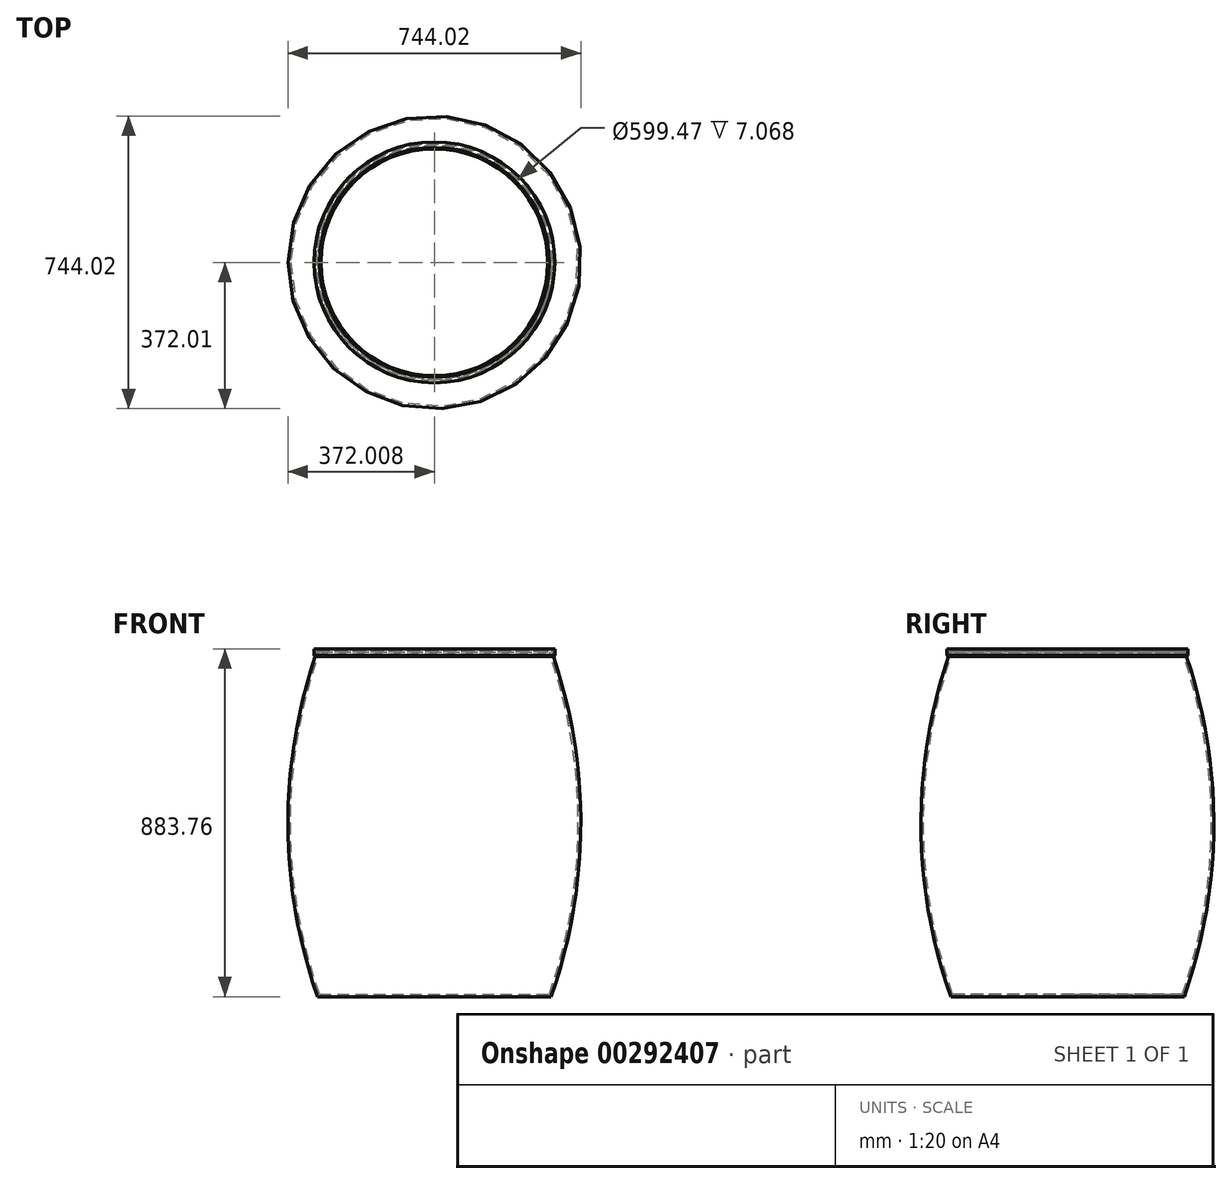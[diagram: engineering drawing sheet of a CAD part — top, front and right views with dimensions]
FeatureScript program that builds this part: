
annotation { "Feature Type Name" : "Feature", "Feature Type Description" : "" }
export const myFeature = defineFeature(function(context is Context, id is Id, definition is map)
    precondition{}
    {
        {
            var Q0;
            Q0=qCreatedBy(makeId("Front.planeOp"),FACE);
            var sketch = newSketch(context, id + "F0", { "sketchPlane" : qUnion([Q0])});
            skLineSegment(sketch, "E0", {"start": v(-396.66, -91.94) * mm, "end": v(466.94, -91.94) * mm});
            skLineSegment(sketch, "E1", {"start": v(466.94, -91.94) * mm, "end": v(466.94, 200.16) * mm});
            skLineSegment(sketch, "E2", {"start": v(-396.66, -91.94) * mm, "end": v(-396.66, 200.16) * mm});
            skLineSegment(sketch, "E3", {"start": v(466.94, 200.16) * mm, "end": v(474.4, 203.75) * mm});
            skLineSegment(sketch, "E4", {"start": v(474.4, 203.75) * mm, "end": v(474.4, 207.8) * mm});
            skLineSegment(sketch, "E5", {"start": v(474.4, 207.8) * mm, "end": v(467.33, 207.8) * mm});
            skLineSegment(sketch, "E6", {"start": v(467.33, 207.8) * mm, "end": v(463.3, 203.17) * mm});
            skArc(sketch, "E7", {"start": v(463.3, 203.17) * mm, "mid": v(33.07, 273.7) * mm, "end": v(-396.66, 200.16) * mm});
            skLineSegment(sketch, "E8.0", {"start": v(-403, -91.94) * mm, "end": v(-403, 204.66) * mm});
            skArc(sketch, "E8.1", {"start": v(461.31, 210.55) * mm, "mid": v(28.66, 280.04) * mm, "end": v(-403, 204.66) * mm});
            skLineSegment(sketch, "E8.2", {"start": v(464.44, 214.14) * mm, "end": v(461.31, 210.55) * mm});
            skLineSegment(sketch, "E8.3", {"start": v(473.3, -91.94) * mm, "end": v(473.3, 196.17) * mm});
            skLineSegment(sketch, "E8.4", {"start": v(473.3, 196.17) * mm, "end": v(480.75, 199.76) * mm});
            skLineSegment(sketch, "E8.5", {"start": v(480.75, 199.76) * mm, "end": v(480.75, 214.14) * mm});
            skLineSegment(sketch, "E8.6", {"start": v(480.75, 214.14) * mm, "end": v(464.44, 214.14) * mm});
            skLineSegment(sketch, "E9", {"start": v(466.94, -91.94) * mm, "end": v(473.3, -91.94) * mm});
            skLineSegment(sketch, "E10", {"start": v(-403, -91.94) * mm, "end": v(-396.66, -91.94) * mm});
            skSolve(sketch);
        }
        {
            var Q0;
            Q0=makeQuery(id+"F0.imprint","IMPRINT",FACE,{"disambiguationData":[TD([[makeQuery(id+"F0.imprint","IMPRINT",EDGE,{"derivedFrom":sQuery(id+"F0.wireOp",EDGE,"E1")}),-1.0]])]});
            var Q1;
            Q1=sQuery(id+"F0.wireOp",EDGE,"E0");
            var Q2;
            Q2=sQuery(id+"F0.wireOp",EDGE,"E0");
            revolve(context, id + "F1", {"entities" : qUnion([Q0]), "surfaceEntities" : qUnion([Q1]), "axis" : qUnion([Q2]), "revolveType" : RevolveType.FULL});
        }
        {
            var Q0;
            Q0=makeQuery(id+"F1.opRevolve","SWEPT_FACE",FACE,{"disambiguationData":[OSD([sQuery(id+"F0.wireOp",EDGE,"E8.0")])]});
            cPlane(context, id + "F2", {"entities" : qUnion([Q0]), "cplaneType" : CPlaneType.OFFSET, "offset" : 0 * mm, "width" : 152.4 * mm, "height" : 152.4 * mm});
        }
        {
            var Q0;
            Q0=qCreatedBy(id+"F2.planeOp",FACE);
            var sketch = newSketch(context, id + "F3", { "sketchPlane" : qUnion([Q0])});
            skLineSegment(sketch, "E11", {"start": v(0, -256.66) * mm, "end": v(-450.3, -256.66) * mm});
            skSolve(sketch);
        }
        {
            var Q0;
            Q0=makeQuery(id+"F1.opRevolve","SWEPT_BODY",BODY,{"disambiguationData":[OSD([sQuery(id+"F0.wireOp",EDGE,"E1"),sQuery(id+"F0.wireOp",EDGE,"E2"),sQuery(id+"F0.wireOp",EDGE,"E3"),sQuery(id+"F0.wireOp",EDGE,"E4"),sQuery(id+"F0.wireOp",EDGE,"E5"),sQuery(id+"F0.wireOp",EDGE,"E6"),sQuery(id+"F0.wireOp",EDGE,"E7"),sQuery(id+"F0.wireOp",EDGE,"E8.0"),sQuery(id+"F0.wireOp",EDGE,"E8.1"),sQuery(id+"F0.wireOp",EDGE,"E8.2"),sQuery(id+"F0.wireOp",EDGE,"E8.3"),sQuery(id+"F0.wireOp",EDGE,"E8.4"),sQuery(id+"F0.wireOp",EDGE,"E8.5"),sQuery(id+"F0.wireOp",EDGE,"E8.6"),sQuery(id+"F0.wireOp",EDGE,"E9"),sQuery(id+"F0.wireOp",EDGE,"E10")])]});
            var Q1;
            Q1=sQuery(id+"F3.wireOp",EDGE,"E11");
            transform(context, id + "F4", {"entities" : qUnion([Q0]), "transformType" : TransformType.ROTATION, "transformAxis" : qUnion([Q1]), "angle" : 90 * degree, "oppositeDirection" : true, "makeCopy" : false});
        }
    });
